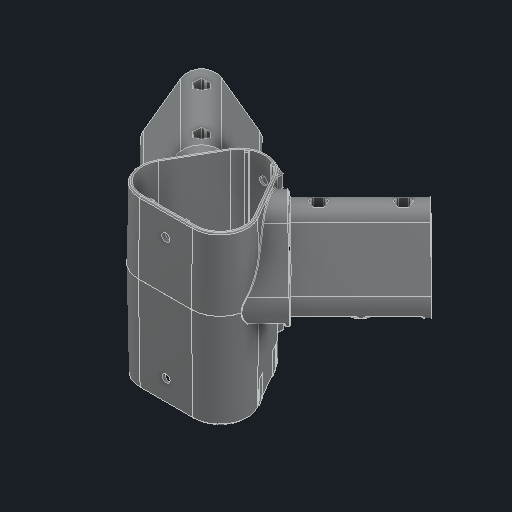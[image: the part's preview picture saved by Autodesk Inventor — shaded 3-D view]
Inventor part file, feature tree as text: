
AUTODESK INVENTOR PART (.ipt)
format: ipt  version: 2025 (Build 290162000, 162)  size: 2,474,496 bytes
history: native  units: in
note: dims shown in document units (in); Inventor stores cm internally (conversion verified against a paired STEP export)
features: mirror x1
ambient origin geometry x8: Origin, YZ Plane, XZ Plane, XY Plane, X Axis, Y Axis, Z Axis, Center Point
bodies: Solid1 (feature_tree)
feature tree (1):
  mirror  "Mirror2"
